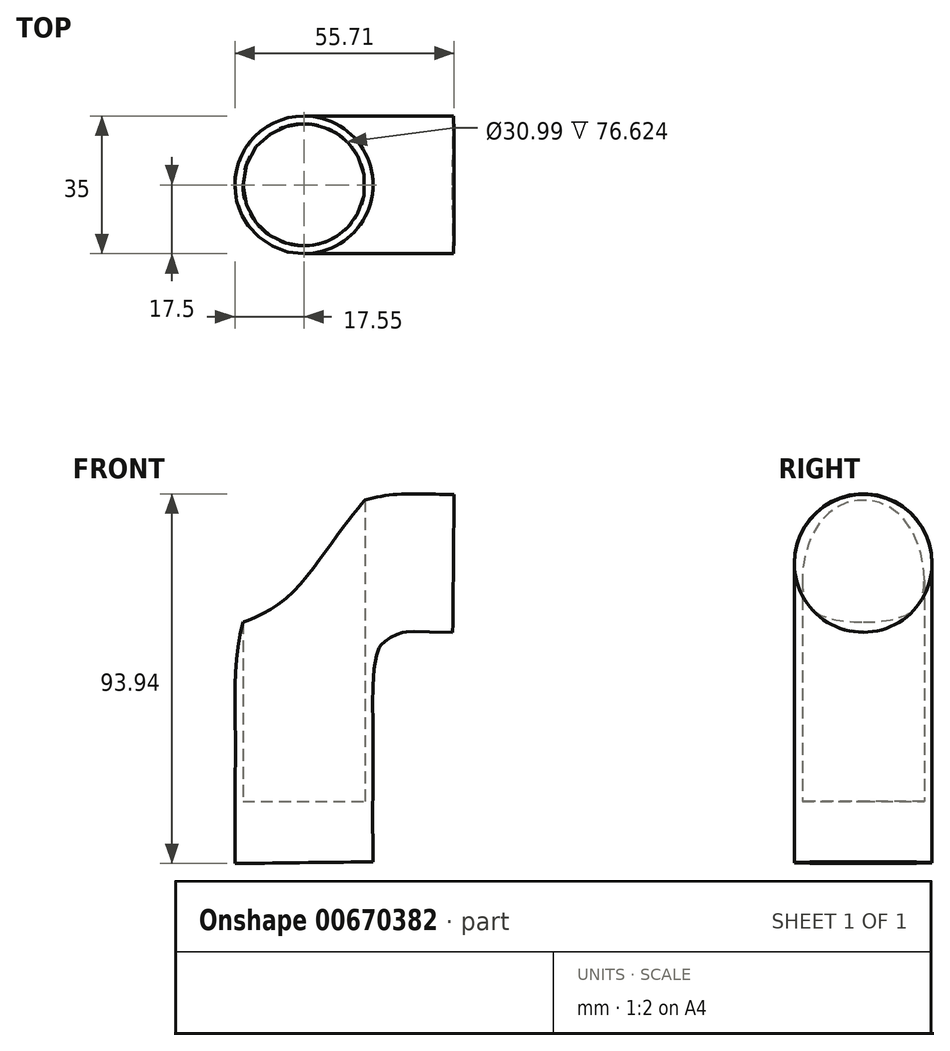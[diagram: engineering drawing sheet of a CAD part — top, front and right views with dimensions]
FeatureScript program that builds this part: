
annotation { "Feature Type Name" : "Feature", "Feature Type Description" : "" }
export const myFeature = defineFeature(function(context is Context, id is Id, definition is map)
    precondition{}
    {
        {
            var Q0;
            Q0=qCreatedBy(makeId("Front.planeOp"),FACE);
            var sketch = newSketch(context, id + "F0", { "sketchPlane" : qUnion([Q0])});
            skFitSpline(sketch, "E0", {"points": [v(37.99, 60.53) * mm, v(19.71, 59.68) * mm, v(3.58, 47.18) * mm, v(0, 18.97) * mm, v(0, 7.85) * mm, v(0, -15.55) * mm], "startDerivative": vector(-146.56, 1.94) * mm, "endDerivative": vector(1.35, -141.54) * mm});
            skSolve(sketch);
        }
        {
            var Q0;
            Q0=qCreatedBy(makeId("Top.planeOp"),FACE);
            var sketch = newSketch(context, id + "F1", { "sketchPlane" : qUnion([Q0])});
            skCircle(sketch, "E1", {"center": v(0, 0) * mm, "radius": 17.5 * mm});
            skLineSegment(sketch, "E2", {"start": v(0, 0) * mm, "end": v(10.92, -13.67) * mm});
            skSolve(sketch);
        }
        {
            var Q0;
            Q0=makeQuery(id+"F1.imprint","IMPRINT",FACE,{"disambiguationData":[TD([[makeQuery(id+"F1.imprint","IMPRINT",EDGE,{"derivedFrom":sQuery(id+"F1.wireOp",EDGE,"E1")}),1.0]])]});
            var Q1;
            Q1=sQuery(id+"F0.wireOp",EDGE,"E0");
            sweep(context, id + "F2", {"profiles" : qUnion([Q0]), "path" : qUnion([Q1])});
        }
        {
            var Q0;
            Q0=sQuery(id+"F1.wireOp",VERTEX,"E1.center");
            var Q1;
            Q1=makeQuery(id+"F2.opSweep","SWEPT_BODY",BODY,{"disambiguationData":[OSD([sQuery(id+"F0.wireOp",EDGE,"E0"),sQuery(id+"F1.wireOp",EDGE,"E1")])]});
            hole(context, id + "F3", {"style" : HoleStyle.C_BORE, "endStyle" : HoleEndStyle.THROUGH, "oppositeDirection" : true, "holeDiameter" : 30.99 * mm, "cBoreDiameter" : 30.99 * mm, "cBoreDepth" : 5 * mm, "majorDiameter" : 5 * mm, "isTappedThrough" : true, "tappedDepth" : 12 * mm, "tapClearance" : 3, "locations" : qUnion([Q0]), "scope" : qUnion([Q1])});
        }
    });
